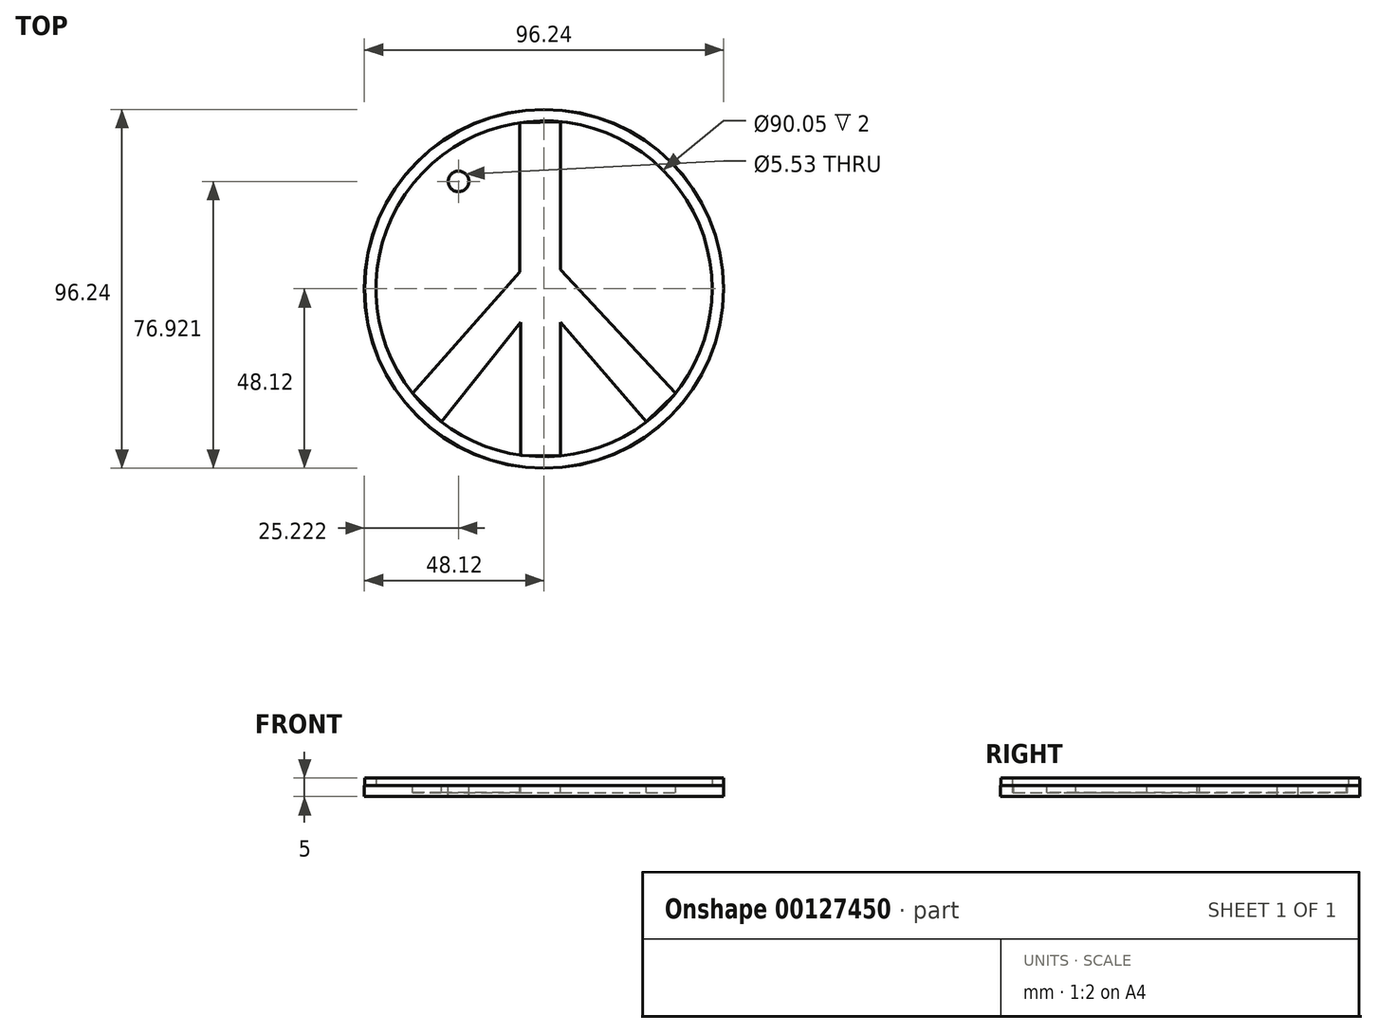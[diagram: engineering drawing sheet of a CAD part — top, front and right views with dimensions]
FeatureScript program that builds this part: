
annotation { "Feature Type Name" : "Feature", "Feature Type Description" : "" }
export const myFeature = defineFeature(function(context is Context, id is Id, definition is map)
    precondition{}
    {
        {
            var Q0;
            Q0=qCreatedBy(makeId("Top.planeOp"),FACE);
            var sketch = newSketch(context, id + "F0", { "sketchPlane" : qUnion([Q0])});
            skCircle(sketch, "E0", {"center": v(0, 0) * mm, "radius": 48.12 * mm});
            skSolve(sketch);
        }
        {
            var Q0;
            Q0 = qSketchRegion(id + "F0", true);
            extrude(context, id + "F1", {"entities" : qUnion([Q0]), "depth" : 3 * mm});
        }
        {
            var Q0;
            Q0=makeQuery(id+"F1.opExtrude","CAP_FACE",FACE,{"disambiguationData":[OSD([sQuery(id+"F0.wireOp",EDGE,"E0")])],"isStart":false});
            var sketch = newSketch(context, id + "F2", { "sketchPlane" : qUnion([Q0])});
            skCircle(sketch, "E1", {"center": v(0, 0) * mm, "radius": 45.02 * mm});
            skCircle(sketch, "E2", {"center": v(0, 0) * mm, "radius": 48.07 * mm});
            skSolve(sketch);
        }
        {
            var Q0;
            Q0 = qSketchRegion(id + "F2", true);
            extrude(context, id + "F3", {"entities" : qUnion([Q0]), "operationType" : NewBodyOperationType.ADD, "depth" : 2 * mm});
        }
        {
            var Q0;
            Q0=makeQuery(id+"F3.boolean.opBoolean","SPLIT",FACE,{"disambiguationData":[TD([makeQuery(id+"F3.opExtrude","SWEPT_FACE",FACE,{"disambiguationData":[OSD([sQuery(id+"F2.wireOp",EDGE,"E1")])]})])],"derivedFrom":makeQuery(id+"F1.opExtrude","CAP_FACE",FACE,{"disambiguationData":[OSD([sQuery(id+"F0.wireOp",EDGE,"E0")])],"isStart":false})});
            var sketch = newSketch(context, id + "F4", { "sketchPlane" : qUnion([Q0])});
            skLineSegment(sketch, "E3", {"start": v(-6.22, -44.6) * mm, "end": v(-6.22, -8.95) * mm});
            skLineSegment(sketch, "E4", {"start": v(-6.22, -8.95) * mm, "end": v(-27.45, -35.69) * mm});
            skLineSegment(sketch, "E5", {"start": v(-35.23, -28.04) * mm, "end": v(-6.45, 4.55) * mm});
            skLineSegment(sketch, "E6", {"start": v(-6.45, 4.55) * mm, "end": v(-6.45, 44.56) * mm});
            skLineSegment(sketch, "E7", {"start": v(4.4, 44.8) * mm, "end": v(4.4, 5.13) * mm});
            skLineSegment(sketch, "E8", {"start": v(4.4, -44.8) * mm, "end": v(4.4, -8.95) * mm});
            skLineSegment(sketch, "E9", {"start": v(4.4, -8.95) * mm, "end": v(27.45, -35.69) * mm});
            skLineSegment(sketch, "E10", {"start": v(4.4, 5.13) * mm, "end": v(35.23, -28.04) * mm});
            skLineSegment(sketch, "E11", {"start": v(-6.45, 44.56) * mm, "end": v(4.4, 44.8) * mm});
            skLineSegment(sketch, "E12", {"start": v(27.45, -35.69) * mm, "end": v(35.23, -28.04) * mm});
            skLineSegment(sketch, "E13", {"start": v(-6.22, -44.6) * mm, "end": v(4.4, -44.8) * mm});
            skLineSegment(sketch, "E14", {"start": v(-27.45, -35.69) * mm, "end": v(-35.23, -28.04) * mm});
            skSolve(sketch);
        }
        {
            var Q0;
            Q0 = qSketchRegion(id + "F4", true);
            extrude(context, id + "F5", {"entities" : qUnion([Q0]), "operationType" : NewBodyOperationType.REMOVE, "oppositeDirection" : true, "depth" : 2 * mm});
        }
        {
            var Q0;
            {var subQ0=makeQuery(id+"F3.opExtrude","SWEPT_FACE",FACE,{"disambiguationData":[OSD([sQuery(id+"F2.wireOp",EDGE,"E1")])]});var subQ1=makeQuery(id+"F1.opExtrude","CAP_FACE",FACE,{"disambiguationData":[OSD([sQuery(id+"F0.wireOp",EDGE,"E0")])],"isStart":false});Q0=makeQuery(id+"F5.boolean.opBoolean","SPLIT",FACE,{"disambiguationData":[TD([subQ1,subQ0,makeQuery(id+"F5.opExtrude","SWEPT_FACE",FACE,{"disambiguationData":[OSD([sQuery(id+"F4.wireOp",EDGE,"E5")])]}),makeQuery(id+"F5.opExtrude","SWEPT_FACE",FACE,{"disambiguationData":[OSD([sQuery(id+"F4.wireOp",EDGE,"E6")])]}),makeQuery(id+"F5.opExtrude","SWEPT_FACE",FACE,{"disambiguationData":[OSD([sQuery(id+"F4.wireOp",EDGE,"E11")])]}),makeQuery(id+"F5.opExtrude","SWEPT_FACE",FACE,{"disambiguationData":[OSD([sQuery(id+"F4.wireOp",EDGE,"E14")])]})])],"derivedFrom":makeQuery(id+"F3.boolean.opBoolean","SPLIT",FACE,{"disambiguationData":[TD([subQ0])],"derivedFrom":subQ1})});}
            var sketch = newSketch(context, id + "F6", { "sketchPlane" : qUnion([Q0])});
            skCircle(sketch, "E15", {"center": v(-22.9, 28.8) * mm, "radius": 2.77 * mm});
            skSolve(sketch);
        }
        {
            var Q0;
            Q0 = qSketchRegion(id + "F6", true);
            extrude(context, id + "F7", {"entities" : qUnion([Q0]), "operationType" : NewBodyOperationType.REMOVE, "oppositeDirection" : true, "depth" : 3 * mm});
        }
    });
